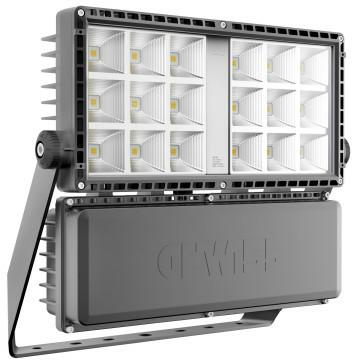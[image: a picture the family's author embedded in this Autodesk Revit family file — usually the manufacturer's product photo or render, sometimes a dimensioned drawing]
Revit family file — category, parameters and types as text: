
# Revit family: Lighting-Floodlights-GEWISS-SMART[PRO]2.0-LED-MEDIUM-POWER_2MODULE_DALI.CLII
name_source: partatom
category: Apparecchi per illuminazione
units: mm (PartAtom-declared; Revit-internal decimal feet)

## family parameters
Condiviso = No
Host = Superficie
Punto di calcolo locali = No
Quota connettore circolare = Usa diametro
Sorgente d'illuminazione = No
Taglio con vuoti quando caricato = No
Tipo di parte = Normale

## types (45) — shared parameters
Applicazione = Indoor / Outdoor
Body = Die-cast aluminium -
Catalogue = LIGHTING
Classification: = -
Colour = Graphite grey
Colour : = Polyester powder coated
Context = Sport, Big Areas
Control System = DALI
DIN 18032-3 certification = Yes
Device with reduced surface temperature = No
Driver = Included
Driver Box = Built-in
Eletrical and lighting features = -
External screw = Stainless steel
Fixing = Bracket
GW - Codice Electrocod = 2424
Gasket = Anti-aging silicone
General information = -
Glow Wire Test : = -
IDF = bc28a6a6-48c2-44be-9680-979c10432a70
IDT = 132314cb1b854b53a35eaeb109d835d9
IP degree = IP66
Immagine tipo = GWP2274AD.jpg
Installationa and maintenance = -
Insulation class = II
LED Maintenance = Not available
Lampada = LED
Lifetime = L90B10 (Tq+25°C) - 40000h L90B10 (Tq+50°C) = 32000h L80B10 (Tq+25°C) - 90000h
Locking Hook = Hexagonal metric screws
Luminaire = LED luminaire with small,mid and high lumen power
Materials = -
Maximum surface exposed to the wind : = 0,170 m2
Mouting and installation = High-mast lighting - Wall mounting - Ground mouting
Operating temperature : = -30 +50 °C
Optic Maintenance = Not available
Optic and illuminating features = -
Overvoltage protection = DM 6 kV / CM 10 kV
Photobiological Risk Class = -
Produttore = GEWISS S.p.A.
Prospetto di default = 1219 mm
Rated frequency (Hz) = 50 / 60
SEO = Floodlight
Shield type = Flat tempered glass 4mm
Shock resistance = IK08
Spostamento_x = 2186 mm
Spostamento_x_effettivo = 1814 mm
Standard- = EN60598-1; EN60598-2-5; IEC 62778; IEC 62471; EN13201
Standards and approvals = -
Stocking temperature = -
Supply voltage = 220 - 240 V
System power = 330W
Technical sheet = https://www.gewiss.com
Tilt- = Rotation on bracket with integrated goniometer
Type of light source = LED - Not replaceable
URL = https://www.gewiss.com
Unique digital code (Datamatrix) = Currently not present
Version file RFA = 20.11
Warranty = 5 years
Weight (kg): = 13
Wiring = Watertight connector

## per-type parameters (varying)
| type | Color Rendering Index | Colour temperature | Descrizione | Efficiency (lm/W) | IPEA | Lumen output (lm) | Modello | Optic | Optic : | Standard Deviation Colour Matching | Unified Glare Rating | Versions |
| GWP2274CB - SMARTPRO2.0 2M 4000K CRI70 A1 DALI CL2 | CRI-70 | 4000K | SMARTPRO2.0 2M 4000K CRI70 A1 DALI CL2 | 115 | ROAD = A // LARGE AREAS = A3 + // CYCLOPEDONALS = A + // GREEN AREAS = A + // HISTORICAL CENTER = A5 + // OTHER = A5 + | 38100 | GWP2274CB | A1 - Asymmetrical Wide | Polished quartz and metallized PC HT reflector | SDCM = 5 | G*4 - ULOR = 0 | 4000K natural light |
| GWP2274NB - SMARTPRO2.0 2M 4000K CRI70 A3 DALI CL2 | CRI-70 | 4000K | SMARTPRO2.0 2M 4000K CRI70 A3 DALI CL2 | 121 | ROAD = A + // LARGE AREAS = A4 + // CICLOPEDONALI = A ++ // GREEN AREAS = A ++ // HISTORICAL CENTER = A6 + // OTHER = A6 + | 39800 | GWP2274NB | A3 - Assymetric Narrow | Polished anodised aluminum reflector with 99.99% pure aluminum | SDCM = 5 | G*6 - ULOR = 0 | 4000K natural light |
| GWP2275FB - SMARTPRO2.0 2M 5700K CRI70 A2 DALI CL2 | CRI-70 | 5700K | SMARTPRO2.0 2M 5700K CRI70 A2 DALI CL2 | 99 | ROAD = C // LARGE AREAS = A + // CYCLOPEDONALS = B // GREEN AREAS = B // HISTORICAL CENTER = A3 + // OTHER = A3 + | 32800 | GWP2275FB | A2 - Asymmetrical Medium | Polished anodised aluminum reflector with 99.99% pure aluminum | SDCM = 5 | G*3 - ULOR = 0 | 5700K cold light |
| GWP2283GB - SMARTPRO2.0 2M 3000K CRI80 C4 DALI CL2 | CRI-80 | 3000K | SMARTPRO2.0 2M 3000K CRI80 C4 DALI CL2 | 108 | ROAD = B // LARGE AREAS = A ++ // CYCLOPEDONALS = A // GREEN AREAS = A // HISTORICAL CENTER = A4 + // OTHER = A4 + | 35500 | GWP2283GB | C4 - Circular 15° | Polished quartz and metallized PC HT reflector | SDCM = 3 | G*6 - ULOR = 0 | 3000K warm light |
| GWP2273AB - SMARTPRO2.0 2M 3000K CRI70 S1 DALI CL2 | CRI-70 | 3000K | SMARTPRO2.0 2M 3000K CRI70 S1 DALI CL2 | 111 | ROAD = A // LARGE AREAS = A ++ // CYCLOPEDONALS = A + // GREEN AREAS = A + // HISTORICAL CENTER = A4 + // OTHER = A4 + | 36600 | GWP2273AB | S1 - Symmetric Wide | Polished quartz and metallized PC HT reflector | SDCM = 5 | G*6 - ULOR = 0 | 3000K warm light |
| GWP2284MB - SMARTPRO2.0 2M 4000K CRI80 C1 DALI CL2 | CRI-80 | 4000K | SMARTPRO2.0 2M 4000K CRI80 C1 DALI CL2 | 113 | ROAD = A // LARGE AREAS = A3 + // CYCLOPEDONALS = A + // GREEN AREAS = A + // HISTORICAL CENTER = A5 + // OTHER = A5 + | 37300 | GWP2284MB | C1 - Circular 30° | Polished quartz and metallized PC HT reflector | SDCM = 3 | G*6 - ULOR = 0 | 4000K natural light |
| GWP2273FB - SMARTPRO2.0 2M 3000K CRI70 A2 DALI CL2 | CRI-70 | 3000K | SMARTPRO2.0 2M 3000K CRI70 A2 DALI CL2 | 93 | ROAD = C // LARGE AREAS = A // CICLOPEDONALI = B // GREEN AREAS = B // HISTORICAL CENTER = A ++ // OTHER = A ++ | 30600 | GWP2273FB | A2 - Asymmetrical Medium | Polished anodised aluminum reflector with 99.99% pure aluminum | SDCM = 5 | G*3 - ULOR = 0 | 3000K warm light |
| GWP2274BB - SMARTPRO2.0 2M 4000K CRI70 S2 DALI CL2 | CRI-70 | 4000K | SMARTPRO2.0 2M 4000K CRI70 S2 DALI CL2 | 123 | ROAD = A + // LARGE AREAS = A4 + // CICLOPEDONALI = A ++ // GREEN AREAS = A ++ // HISTORICAL CENTER = A6 + // OTHER = A6 + | 40600 | GWP2274BB | S2 - Symmetric Medium | Polished anodised aluminum reflector with 99.99% pure aluminum | SDCM = 5 | G*6 - ULOR = 0 | 4000K natural light |
| GWP2275NB - SMARTPRO2.0 2M 5700K CRI70 A3 DALI CL2 | CRI-70 | 5700K | SMARTPRO2.0 2M 5700K CRI70 A3 DALI CL2 | 121 | ROAD = A + // LARGE AREAS = A4 + // CICLOPEDONALI = A ++ // GREEN AREAS = A ++ // HISTORICAL CENTER = A6 + // OTHER = A6 + | 39800 | GWP2275NB | A3 - Assymetric Narrow | Polished anodised aluminum reflector with 99.99% pure aluminum | SDCM = 5 | G*6 - ULOR = 0 | 5700K cold light |
| GWP2273LB - SMARTPRO2.0 2M 3000K CRI70 C2 DALI CL2 | CRI-70 | 3000K | SMARTPRO2.0 2M 3000K CRI70 C2 DALI CL2 | 113 | ROAD = A // LARGE AREAS = A3 + // CYCLOPEDONALS = A + // GREEN AREAS = A + // HISTORICAL CENTER = A5 + // OTHER = A5 + | 37300 | GWP2273LB | C2 - Circular 25° | Polished quartz and metallized PC HT reflector | SDCM = 5 | G*6 - ULOR = 0 | 3000K warm light |
| GWP2284AB - SMARTPRO2.0 2M 4000K CRI80 S1 DALI CL2 | CRI-80 | 4000K | SMARTPRO2.0 2M 4000K CRI80 S1 DALI CL2 | 111 | ROAD = A // LARGE AREAS = A ++ // CYCLOPEDONALS = A + // GREEN AREAS = A + // HISTORICAL CENTER = A4 + // OTHER = A4 + | 36600 | GWP2284AB | S1 - Symmetric Wide | Polished quartz and metallized PC HT reflector | SDCM = 3 | G*6 - ULOR = 0 | 4000K natural light |
| GWP2275MB - SMARTPRO2.0 2M 5700K CRI70 C1 DALI CL2 | CRI-70 | 5700K | SMARTPRO2.0 2M 5700K CRI70 C1 DALI CL2 | 121 | ROAD = A + // LARGE AREAS = A4 + // CICLOPEDONALI = A ++ // GREEN AREAS = A ++ // HISTORICAL CENTER = A6 + // OTHER = A6 + | 40000 | GWP2275MB | C1 - Circular 30° | Polished quartz and metallized PC HT reflector | SDCM = 5 | G*6 - ULOR = 0 | 5700K cold light |
| GWP2273BB - SMARTPRO2.0 2M 3000K CRI70 S2 DALI CL2 | CRI-70 | 3000K | SMARTPRO2.0 2M 3000K CRI70 S2 DALI CL2 | 115 | ROAD = A // LARGE AREAS = A3 + // CYCLOPEDONALS = A + // GREEN AREAS = A + // HISTORICAL CENTER = A5 + // OTHER = A5 + | 37900 | GWP2273BB | S2 - Symmetric Medium | Polished anodised aluminum reflector with 99.99% pure aluminum | SDCM = 5 | G*6 - ULOR = 0 | 3000K warm light |
| GWP2273MB - SMARTPRO2.0 2M 3000K CRI70 C1 DALI CL2 | CRI-70 | 3000K | SMARTPRO2.0 2M 3000K CRI70 C1 DALI CL2 | 113 | ROAD = A // LARGE AREAS = A3 + // CYCLOPEDONALS = A + // GREEN AREAS = A + // HISTORICAL CENTER = A5 + // OTHER = A5 + | 37300 | GWP2273MB | C1 - Circular 30° | Polished quartz and metallized PC HT reflector | SDCM = 5 | G*6 - ULOR = 0 | 3000K warm light |
| GWP2275GB - SMARTPRO2.0 2M 5700K CRI70 C4 DALI CL2 | CRI-70 | 5700K | SMARTPRO2.0 2M 5700K CRI70 C4 DALI CL2 | 124 | ROAD = A + // LARGE AREAS = A4 + // CICLOPEDONALI = A ++ // GREEN AREAS = A ++ // HISTORICAL CENTER = A6 + // OTHER = A6 + | 40900 | GWP2275GB | C4 - Circular 15° | Polished quartz and metallized PC HT reflector | SDCM = 5 | G*6 - ULOR = 0 | 5700K cold light |
| GWP2283AB - SMARTPRO2.0 2M 3000K CRI80 S1 DALI CL2 | CRI-80 | 3000K | SMARTPRO2.0 2M 3000K CRI80 S1 DALI CL2 | 103 | ROAD = B // LARGE AREAS = A + // CYCLOPEDONALS = A // GREEN AREAS = A // HISTORICAL CENTER = A3 + // OTHER = A3 + | 34000 | GWP2283AB | S1 - Symmetric Wide | Polished quartz and metallized PC HT reflector | SDCM = 3 | G*6 - ULOR = 0 | 3000K warm light |
| GWP2284FB - SMARTPRO2.0 2M 4000K CRI80 A2 DALI CL2 | CRI-80 | 4000K | SMARTPRO2.0 2M 4000K CRI80 A2 DALI CL2 | 93 | ROAD = C // LARGE AREAS = A // CICLOPEDONALI = B // GREEN AREAS = B // HISTORICAL CENTER = A ++ // OTHER = A ++ | 30600 | GWP2284FB | A2 - Asymmetrical Medium | Polished anodised aluminum reflector with 99.99% pure aluminum | SDCM = 3 | G*3 - ULOR = 0 | 4000K natural light |
| GWP2283HB - SMARTPRO2.0 2M 3000K CRI80 C3 DALI CL2 | CRI-80 | 3000K | SMARTPRO2.0 2M 3000K CRI80 C3 DALI CL2 | 108 | ROAD = B // LARGE AREAS = A ++ // CYCLOPEDONALS = A // GREEN AREAS = A // HISTORICAL CENTER = A4 + // OTHER = A4 + | 35500 | GWP2283HB | C3 - Circular 20° | Polished quartz and metallized PC HT reflector | SDCM = 3 | G*6 - ULOR = 0 | 3000K warm light |
| GWP2274MB - SMARTPRO2.0 2M 4000K CRI70 C1 DALI CL2 | CRI-70 | 4000K | SMARTPRO2.0 2M 4000K CRI70 C1 DALI CL2 | 121 | ROAD = A + // LARGE AREAS = A4 + // CICLOPEDONALI = A ++ // GREEN AREAS = A ++ // HISTORICAL CENTER = A6 + // OTHER = A6 + | 40000 | GWP2274MB | C1 - Circular 30° | Polished quartz and metallized PC HT reflector | SDCM = 5 | G*6 - ULOR = 0 | 4000K natural light |
| GWP2273HB - SMARTPRO2.0 2M 3000K CRI70 C3 DALI CL2 | CRI-70 | 3000K | SMARTPRO2.0 2M 3000K CRI70 C3 DALI CL2 | 116 | ROAD = A // LARGE AREAS = A3 + // CYCLOPEDONALS = A + // GREEN AREAS = A + // HISTORICAL CENTER = A5 + // OTHER = A5 + | 38200 | GWP2273HB | C3 - Circular 20° | Polished quartz and metallized PC HT reflector | SDCM = 5 | G*6 - ULOR = 0 | 3000K warm light |
| GWP2284CB - SMARTPRO2.0 2M 4000K CRI80 A1 DALI CL2 | CRI-80 | 4000K | SMARTPRO2.0 2M 4000K CRI80 A1 DALI CL2 | 108 | ROAD = B // LARGE AREAS = A ++ // CYCLOPEDONALS = A // GREEN AREAS = A // HISTORICAL CENTER = A4 + // OTHER = A4 + | 35600 | GWP2284CB | A1 - Asymmetrical Wide | Polished quartz and metallized PC HT reflector | SDCM = 3 | G*4 - ULOR = 0 | 4000K natural light |
| GWP2284BB - SMARTPRO2.0 2M 4000K CRI80 S2 DALI CL2 | CRI-80 | 4000K | SMARTPRO2.0 2M 4000K CRI80 S2 DALI CL2 | 115 | ROAD = A // LARGE AREAS = A3 + // CYCLOPEDONALS = A + // GREEN AREAS = A + // HISTORICAL CENTER = A5 + // OTHER = A5 + | 37900 | GWP2284BB | S2 - Symmetric Medium | Polished anodised aluminum reflector with 99.99% pure aluminum | SDCM = 3 | G*6 - ULOR = 0 | 4000K natural light |
| GWP2283BB - SMARTPRO2.0 2M 3000K CRI80 S2 DALI CL2 | CRI-80 | 3000K | SMARTPRO2.0 2M 3000K CRI80 S2 DALI CL2 | 107 | ROAD = B // LARGE AREAS = A ++ // CYCLOPEDONALS = A // GREEN AREAS = A // HISTORICAL CENTER = A4 + // OTHER = A4 + | 35200 | GWP2283BB | S2 - Symmetric Medium | Polished anodised aluminum reflector with 99.99% pure aluminum | SDCM = 3 | G*6 - ULOR = 0 | 3000K warm light |
| GWP2273NB - SMARTPRO2.0 2M 3000K CRI70 A3 DALI CL2 | CRI-70 | 3000K | SMARTPRO2.0 2M 3000K CRI70 A3 DALI CL2 | 113 | ROAD = A // LARGE AREAS = A3 + // CYCLOPEDONALS = A + // GREEN AREAS = A + // HISTORICAL CENTER = A5 + // OTHER = A5 + | 37200 | GWP2273NB | A3 - Assymetric Narrow | Polished anodised aluminum reflector with 99.99% pure aluminum | SDCM = 5 | G*6 - ULOR = 0 | 3000K warm light |
| GWP2284NB - SMARTPRO2.0 2M 4000K CRI80 A3 DALI CL2 | CRI-80 | 4000K | SMARTPRO2.0 2M 4000K CRI80 A3 DALI CL2 | 113 | ROAD = A // LARGE AREAS = A3 + // CYCLOPEDONALS = A + // GREEN AREAS = A + // HISTORICAL CENTER = A5 + // OTHER = A5 + | 37200 | GWP2284NB | A3 - Assymetric Narrow | Polished anodised aluminum reflector with 99.99% pure aluminum | SDCM = 3 | G*6 - ULOR = 0 | 4000K natural light |
| GWP2273GB - SMARTPRO2.0 2M 3000K CRI70 C4 DALI CL2 | CRI-70 | 3000K | SMARTPRO2.0 2M 3000K CRI70 C4 DALI CL2 | 116 | ROAD = A // LARGE AREAS = A3 + // CYCLOPEDONALS = A + // GREEN AREAS = A + // HISTORICAL CENTER = A5 + // OTHER = A5 + | 38200 | GWP2273GB | C4 - Circular 15° | Polished quartz and metallized PC HT reflector | SDCM = 5 | G*6 - ULOR = 0 | 3000K warm light |
| GWP2283NB - SMARTPRO2.0 2M 3000K CRI80 A3 DALI CL2 | CRI-80 | 3000K | SMARTPRO2.0 2M 3000K CRI80 A3 DALI CL2 | 105 | ROAD = B // LARGE AREAS = A ++ // CYCLOPEDONALS = A // GREEN AREAS = A // HISTORICAL CENTER = A3 + // OTHER = A3 + | 34500 | GWP2283NB | A3 - Assymetric Narrow | Polished anodised aluminum reflector with 99.99% pure aluminum | SDCM = 3 | G*6 - ULOR = 0 | 3000K warm light |
| GWP2284GB - SMARTPRO2.0 2M 4000K CRI80 C4 DALI CL2 | CRI-80 | 4000K | SMARTPRO2.0 2M 4000K CRI80 C4 DALI CL2 | 116 | ROAD = A // LARGE AREAS = A3 + // CYCLOPEDONALS = A + // GREEN AREAS = A + // HISTORICAL CENTER = A5 + // OTHER = A5 + | 38200 | GWP2284GB | C4 - Circular 15° | Polished quartz and metallized PC HT reflector | SDCM = 3 | G*6 - ULOR = 0 | 4000K natural light |
| GWP2283CB - SMARTPRO2.0 2M 3000K CRI80 A1 DALI CL2 | CRI-80 | 3000K | SMARTPRO2.0 2M 3000K CRI80 A1 DALI CL2 | 100 | ROAD = B // LARGE AREAS = A + // CYCLOPEDONALS = B // GREEN AREAS = B // HISTORICAL CENTER = A3 + // OTHER = A3 + | 33000 | GWP2283CB | A1 - Asymmetrical Wide | Polished quartz and metallized PC HT reflector | SDCM = 3 | G*4 - ULOR = 0 | 3000K warm light |
| GWP2284HB - SMARTPRO2.0 2M 4000K CRI80 C3 DALI CL2 | CRI-80 | 4000K | SMARTPRO2.0 2M 4000K CRI80 C3 DALI CL2 | 116 | ROAD = A // LARGE AREAS = A3 + // CYCLOPEDONALS = A + // GREEN AREAS = A + // HISTORICAL CENTER = A5 + // OTHER = A5 + | 38200 | GWP2284HB | C3 - Circular 20° | Polished quartz and metallized PC HT reflector | SDCM = 3 | G*6 - ULOR = 0 | 4000K natural light |
| GWP2283LB - SMARTPRO2.0 2M 3000K CRI80 C2 DALI CL2 | CRI-80 | 3000K | SMARTPRO2.0 2M 3000K CRI80 C2 DALI CL2 | 105 | ROAD = B // LARGE AREAS = A ++ // CYCLOPEDONALS = A // GREEN AREAS = A // HISTORICAL CENTER = A3 + // OTHER = A3 + | 34700 | GWP2283LB | C2 - Circular 25° | Polished quartz and metallized PC HT reflector | SDCM = 3 | G*6 - ULOR = 0 | 3000K warm light |
| GWP2274HB - SMARTPRO2.0 2M 4000K CRI70 C3 DALI CL2 | CRI-70 | 4000K | SMARTPRO2.0 2M 4000K CRI70 C3 DALI CL2 | 124 | ROAD = A + // LARGE AREAS = A4 + // CICLOPEDONALI = A ++ // GREEN AREAS = A ++ // HISTORICAL CENTER = A6 + // OTHER = A6 + | 40900 | GWP2274HB | C3 - Circular 20° | Polished quartz and metallized PC HT reflector | SDCM = 5 | G*6 - ULOR = 0 | 4000K natural light |
| GWP2283FB - SMARTPRO2.0 2M 3000K CRI80 A2 DALI CL2 | CRI-80 | 3000K | SMARTPRO2.0 2M 3000K CRI80 A2 DALI CL2 | 86 | ROAD = C // LARGE AREAS = B // CYCLOPEDONALS = C // GREEN AREAS = C // HISTORICAL CENTER = A + // OTHER = A + | 28400 | GWP2283FB | A2 - Asymmetrical Medium | Polished anodised aluminum reflector with 99.99% pure aluminum | SDCM = 3 | G*3 - ULOR = 0 | 3000K warm light |
| GWP2273CB - SMARTPRO2.0 2M 3000K CRI70 A1 DALI CL2 | CRI-70 | 3000K | SMARTPRO2.0 2M 3000K CRI70 A1 DALI CL2 | 108 | ROAD = B // LARGE AREAS = A ++ // CYCLOPEDONALS = A // GREEN AREAS = A // HISTORICAL CENTER = A4 + // OTHER = A4 + | 35600 | GWP2273CB | A1 - Asymmetrical Wide | Polished quartz and metallized PC HT reflector | SDCM = 5 | G*4 - ULOR = 0 | 3000K warm light |
| GWP2274AB - SMARTPRO2.0 2M 4000K CRI70 S1 DALI CL2 | CRI-70 | 4000K | SMARTPRO2.0 2M 4000K CRI70 S1 DALI CL2 | 119 | ROAD = A // LARGE AREAS = A3 + // CYCLOPEDONALS = A + // GREEN AREAS = A + // HISTORICAL CENTER = A6 + // OTHER = A6 + | 39200 | GWP2274AB | S1 - Symmetric Wide | Polished quartz and metallized PC HT reflector | SDCM = 5 | G*6 - ULOR = 0 | 4000K natural light |
| GWP2275CB - SMARTPRO2.0 2M 5700K CRI70 A1 DALI CL2 | CRI-70 | 5700K | SMARTPRO2.0 2M 5700K CRI70 A1 DALI CL2 | 115 | ROAD = A // LARGE AREAS = A3 + // CYCLOPEDONALS = A + // GREEN AREAS = A + // HISTORICAL CENTER = A5 + // OTHER = A5 + | 38100 | GWP2275CB | A1 - Asymmetrical Wide | Polished quartz and metallized PC HT reflector | SDCM = 5 | G*4 - ULOR = 0 | 5700K cold light |
| GWP2284LB - SMARTPRO2.0 2M 4000K CRI80 C2 DALI CL2 | CRI-80 | 4000K | SMARTPRO2.0 2M 4000K CRI80 C2 DALI CL2 | 113 | ROAD = A // LARGE AREAS = A3 + // CYCLOPEDONALS = A + // GREEN AREAS = A + // HISTORICAL CENTER = A5 + // OTHER = A5 + | 37300 | GWP2284LB | C2 - Circular 25° | Polished quartz and metallized PC HT reflector | SDCM = 3 | G*6 - ULOR = 0 | 4000K natural light |
| GWP2283MB - SMARTPRO2.0 2M 3000K CRI80 C1 DALI CL2 | CRI-80 | 3000K | SMARTPRO2.0 2M 3000K CRI80 C1 DALI CL2 | 105 | ROAD = B // LARGE AREAS = A ++ // CYCLOPEDONALS = A // GREEN AREAS = A // HISTORICAL CENTER = A3 + // OTHER = A3 + | 34700 | GWP2283MB | C1 - Circular 30° | Polished quartz and metallized PC HT reflector | SDCM = 3 | G*6 - ULOR = 0 | 3000K warm light |
| GWP2275HB - SMARTPRO2.0 2M 5700K CRI70 C3 DALI CL2 | CRI-70 | 5700K | SMARTPRO2.0 2M 5700K CRI70 C3 DALI CL2 | 124 | ROAD = A + // LARGE AREAS = A4 + // CICLOPEDONALI = A ++ // GREEN AREAS = A ++ // HISTORICAL CENTER = A6 + // OTHER = A6 + | 40900 | GWP2275HB | C3 - Circular 20° | Polished quartz and metallized PC HT reflector | SDCM = 5 | G*6 - ULOR = 0 | 5700K cold light |
| GWP2274FB - SMARTPRO2.0 2M 4000K CRI70 A2 DALI CL2 | CRI-70 | 4000K | SMARTPRO2.0 2M 4000K CRI70 A2 DALI CL2 | 99 | ROAD = C // LARGE AREAS = A + // CYCLOPEDONALS = B // GREEN AREAS = B // HISTORICAL CENTER = A3 + // OTHER = A3 + | 32800 | GWP2274FB | A2 - Asymmetrical Medium | Polished anodised aluminum reflector with 99.99% pure aluminum | SDCM = 5 | G*3 - ULOR = 0 | 4000K natural light |
| GWP2275AB - SMARTPRO2.0 2M 5700K CRI70 S1 DALI CL2 | CRI-70 | 5700K | SMARTPRO2.0 2M 5700K CRI70 S1 DALI CL2 | 119 | ROAD = A // LARGE AREAS = A3 + // CYCLOPEDONALS = A + // GREEN AREAS = A + // HISTORICAL CENTER = A6 + // OTHER = A6 + | 39200 | GWP2275AB | S1 - Symmetric Wide | Polished quartz and metallized PC HT reflector | SDCM = 5 | G*6 - ULOR = 0 | 5700K cold light |
| GWP2275LB - SMARTPRO2.0 2M 5700K CRI70 C2 DALI CL2 | CRI-70 | 5700K | SMARTPRO2.0 2M 5700K CRI70 C2 DALI CL2 | 121 | ROAD = A + // LARGE AREAS = A4 + // CICLOPEDONALI = A ++ // GREEN AREAS = A ++ // HISTORICAL CENTER = A6 + // OTHER = A6 + | 40000 | GWP2275LB | C2 - Circular 25° | Polished quartz and metallized PC HT reflector | SDCM = 5 | G*6 - ULOR = 0 | 5700K cold light |
| GWP2274LB - SMARTPRO2.0 2M 4000K CRI70 C2 DALI CL2 | CRI-70 | 4000K | SMARTPRO2.0 2M 4000K CRI70 C2 DALI CL2 | 121 | ROAD = A + // LARGE AREAS = A4 + // CICLOPEDONALI = A ++ // GREEN AREAS = A ++ // HISTORICAL CENTER = A6 + // OTHER = A6 + | 40000 | GWP2274LB | C2 - Circular 25° | Polished quartz and metallized PC HT reflector | SDCM = 5 | G*6 - ULOR = 0 | 4000K natural light |
| GWP2274GB - SMARTPRO2.0 2M 4000K CRI70 C4 DALI CL2 | CRI-70 | 4000K | SMARTPRO2.0 2M 4000K CRI70 C4 DALI CL2 | 124 | ROAD = A + // LARGE AREAS = A4 + // CICLOPEDONALI = A ++ // GREEN AREAS = A ++ // HISTORICAL CENTER = A6 + // OTHER = A6 + | 40900 | GWP2274GB | C4 - Circular 15° | Polished quartz and metallized PC HT reflector | SDCM = 5 | G*6 - ULOR = 0 | 4000K natural light |
| GWP2275BB - SMARTPRO2.0 2M 5700K CRI70 S2 DALI CL2 | CRI-70 | 5700K | SMARTPRO2.0 2M 5700K CRI70 S2 DALI CL2 | 123 | ROAD = A + // LARGE AREAS = A4 + // CICLOPEDONALI = A ++ // GREEN AREAS = A ++ // HISTORICAL CENTER = A6 + // OTHER = A6 + | 40600 | GWP2275BB | S2 - Symmetric Medium | Polished anodised aluminum reflector with 99.99% pure aluminum | SDCM = 5 | G*6 - ULOR = 0 | 5700K cold light |
